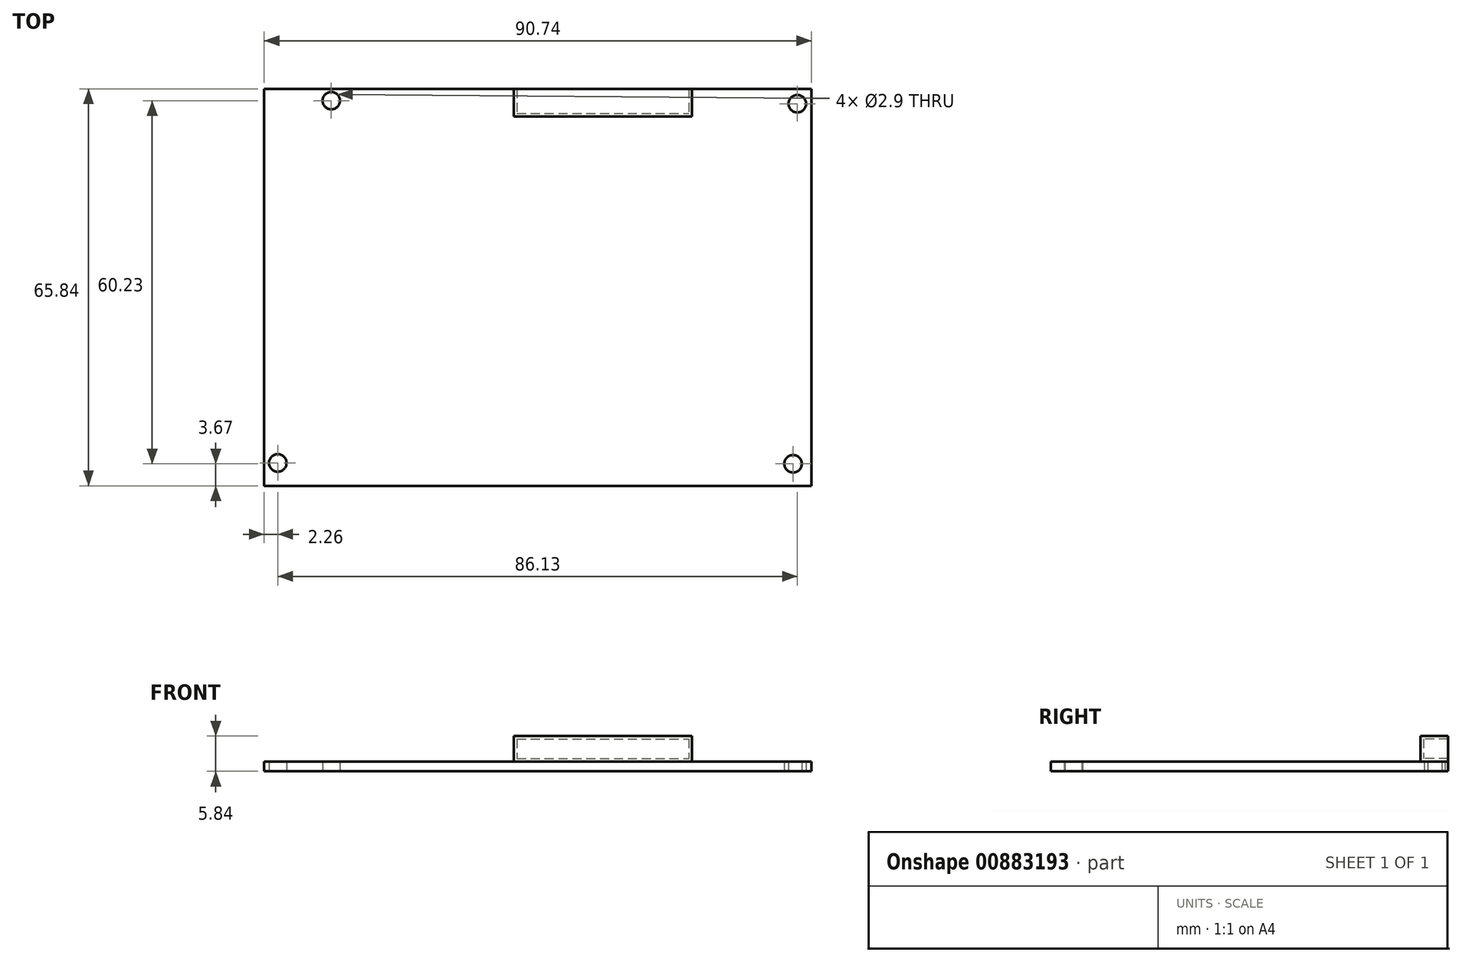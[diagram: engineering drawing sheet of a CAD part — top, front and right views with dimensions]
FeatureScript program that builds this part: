
annotation { "Feature Type Name" : "Feature", "Feature Type Description" : "" }
export const myFeature = defineFeature(function(context is Context, id is Id, definition is map)
    precondition{}
    {
        {
            var Q0;
            Q0=qCreatedBy(makeId("Top.planeOp"),FACE);
            var sketch = newSketch(context, id + "F0", { "sketchPlane" : qUnion([Q0])});
            skLineSegment(sketch, "E0.bottom", {"start": v(0, 0) * mm, "end": v(90.74, 0) * mm});
            skLineSegment(sketch, "E0.top", {"start": v(0, 65.84) * mm, "end": v(90.74, 65.84) * mm});
            skLineSegment(sketch, "E0.left", {"start": v(0, 0) * mm, "end": v(0, 65.84) * mm});
            skLineSegment(sketch, "E0.right", {"start": v(90.74, 0) * mm, "end": v(90.74, 65.84) * mm});
            skCircle(sketch, "E1", {"center": v(11.13, 63.9) * mm, "radius": 1.45 * mm});
            skCircle(sketch, "E2", {"center": v(2.26, 3.81) * mm, "radius": 1.45 * mm});
            skCircle(sketch, "E3", {"center": v(88.39, 63.4) * mm, "radius": 1.45 * mm});
            skCircle(sketch, "E4", {"center": v(87.69, 3.67) * mm, "radius": 1.45 * mm});
            skSolve(sketch);
        }
        {
            var Q0;
            Q0=makeQuery(id+"F0.imprint","IMPRINT",FACE,{"disambiguationData":[TD([[makeQuery(id+"F0.imprint","IMPRINT",EDGE,{"derivedFrom":sQuery(id+"F0.wireOp",EDGE,"E0.bottom")}),1.0]])]});
            extrude(context, id + "F1", {"entities" : qUnion([Q0]), "depth" : 1.6 * mm, "offsetDistance" : 25 * mm});
        }
        {
            var Q0;
            Q0=makeQuery(id+"F1.opExtrude","CAP_FACE",FACE,{"disambiguationData":[OSD([sQuery(id+"F0.wireOp",EDGE,"E0.bottom"),sQuery(id+"F0.wireOp",EDGE,"E0.top"),sQuery(id+"F0.wireOp",EDGE,"E0.left"),sQuery(id+"F0.wireOp",EDGE,"E0.right"),sQuery(id+"F0.wireOp",EDGE,"E1"),sQuery(id+"F0.wireOp",EDGE,"E2"),sQuery(id+"F0.wireOp",EDGE,"E3"),sQuery(id+"F0.wireOp",EDGE,"E4")])],"isStart":false});
            var sketch = newSketch(context, id + "F2", { "sketchPlane" : qUnion([Q0])});
            skLineSegment(sketch, "E5.bottom", {"start": v(41.4, 65.84) * mm, "end": v(70.9, 65.84) * mm});
            skLineSegment(sketch, "E5.top", {"start": v(41.4, 61.28) * mm, "end": v(70.9, 61.28) * mm});
            skLineSegment(sketch, "E5.left", {"start": v(41.4, 65.84) * mm, "end": v(41.4, 61.28) * mm});
            skLineSegment(sketch, "E5.right", {"start": v(70.9, 65.84) * mm, "end": v(70.9, 61.28) * mm});
            skSolve(sketch);
        }
        {
            var Q0;
            Q0 = qSketchRegion(id + "F2", true);
            extrude(context, id + "F3", {"entities" : qUnion([Q0]), "depth" : 4.24 * mm, "offsetDistance" : 25 * mm});
        }
        {
            var Q0;
            Q0=makeQuery(id+"F3.opExtrude","SWEPT_FACE",FACE,{"disambiguationData":[OSD([sQuery(id+"F2.wireOp",EDGE,"E5.bottom")])]});
            shell(context, id + "F4", {"entities" : qUnion([Q0]), "thickness" : 0.5 * mm});
        }
    });
